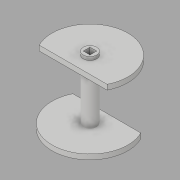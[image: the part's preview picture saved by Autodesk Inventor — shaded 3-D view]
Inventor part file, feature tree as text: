
AUTODESK INVENTOR PART (.ipt)
format: ipt  version: 2017 (Build 210142000, 142)  size: 112,128 bytes
history: native  units: mm
features: extrude x4, sketch x4, plane x1
ambient origin geometry x8: Origin, YZ Plane, XZ Plane, XY Plane, X Axis, Y Axis, Z Axis, Center Point
bodies: Solid1 (feature_tree), Solid2 (feature_tree)
feature tree (9):
  extrude  "Extrusion1"  Depth=4.0mm
  plane  "Work Plane5"
  extrude  "Extrusion4"  Depth=40.0mm TaperAngle=0.0deg
  extrude  "Extrusion5"  Depth=3.0mm TaperAngle=0.0deg
  extrude  "Extrusion3"  Depth=5.0mm
  sketch  "Sketch1"  dims[d0=40.0mm d1=0.0mm d5=4.0mm]
  sketch  "Sketch3"  dims[d6=4.0mm d7=40.0mm d8=0.0mm]
  sketch  "Sketch5"  dims[d13=3.0mm d14=0.0mm d15=3.0mm d16=0.0mm]
  sketch  "Sketch6"  dims[d17=5.0mm d18=0.0mm d19=45.0mm d20=45.0mm]
